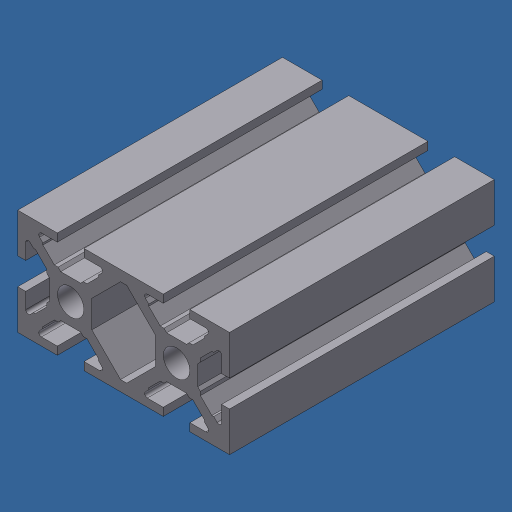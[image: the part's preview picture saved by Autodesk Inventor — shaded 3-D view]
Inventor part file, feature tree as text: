
AUTODESK INVENTOR PART (.ipt)
format: ipt  version: 2024.3 (Build 283343000, 343)  size: 383,488 bytes
history: native  units: mm (DEFAULTED — no unit token found)
features: extrude x4, sketch x3, other x1, mirror x1
ambient origin geometry x8: Origin, YZ Plane, XZ Plane, XY Plane, X Axis, Y Axis, Z Axis, Center Point
bodies: Body1 (feature_tree)
feature tree (9):
  other  "Finish - None"
  extrude  "MK, 40X80"  Depth=14.95mm
  extrude  "Extrusion2"  Depth=3.0mm
  mirror  "Mirror1"
  extrude  "Extrusion3"  Depth=4.0mm
  extrude  "Extrusion4"  Depth=4.0mm
  sketch  "Sketch1"  dims[d0=10.0mm d3=14.95mm]
  sketch  "Sketch2"  dims[d4=14.95mm d5=3.0mm]
  sketch  "Sketch3"  dims[d7=2.0mm d8=4.0mm d9=4.0mm d10=8.949804mm d11=8.949804mm d12=45.0deg d16=8.0mm d17=8.0mm d18=2.5mm d19=20.0mm d21=1.0mm d22=100.0mm d23=0.0mm d24=0.5mm d25=0.5mm d26=1.0mm d28=4.0mm d29=0.5mm d30=10.5mm d31=10.5mm d32=100.0mm d33=0.0mm d34=24.0mm d35=32.0mm d36=10.3432mm d37=12.0mm d38=16.0mm d39=10.0mm d40=0.0mm d41=10.0mm d42=0.0mm]
